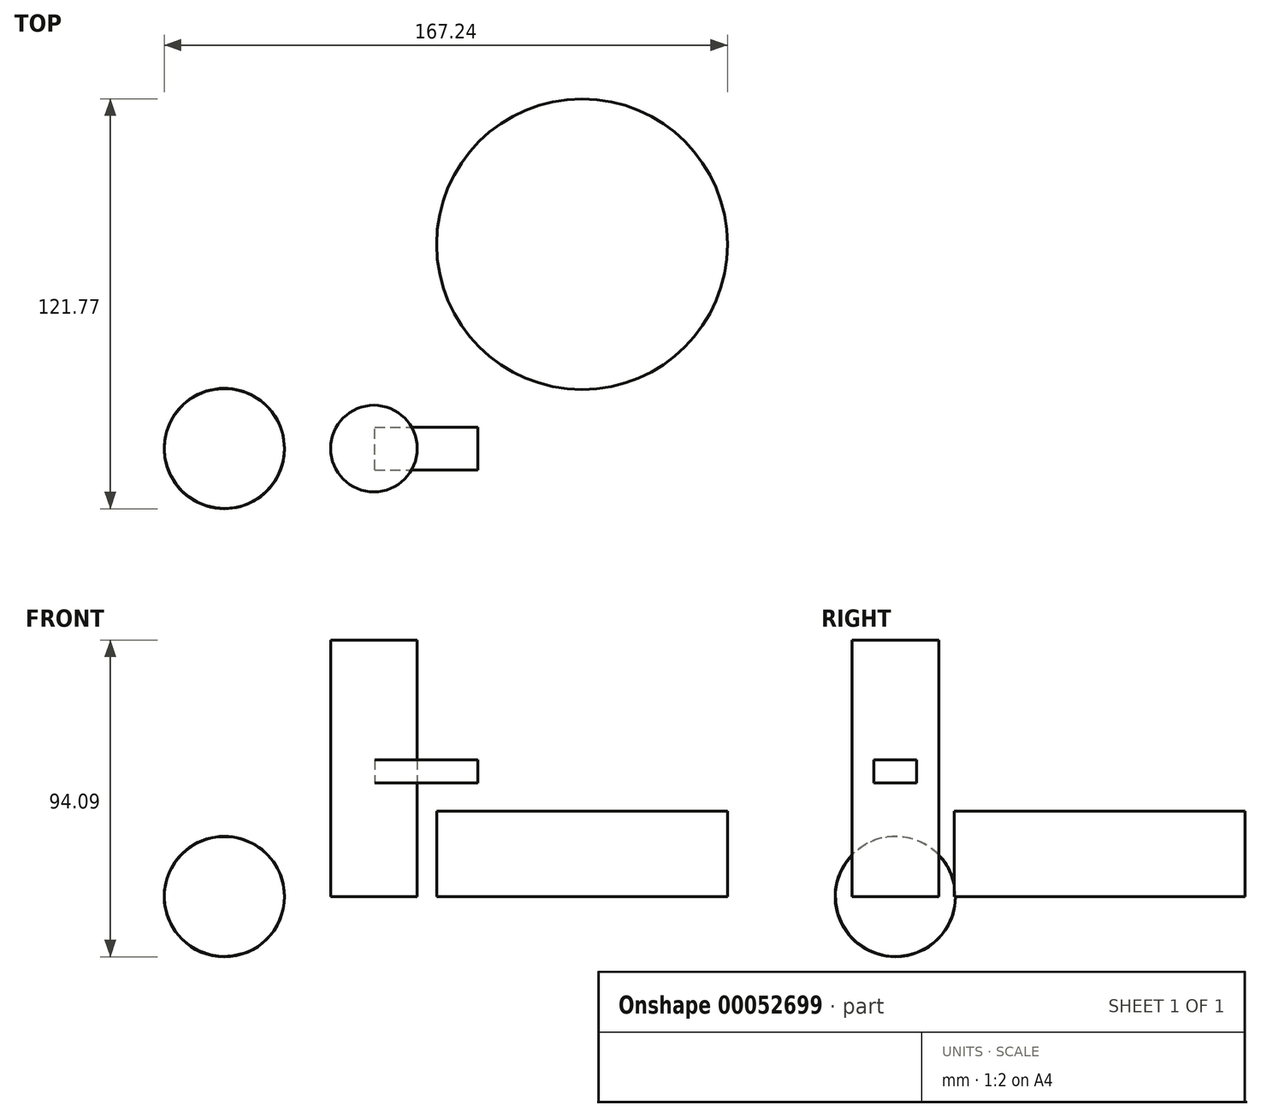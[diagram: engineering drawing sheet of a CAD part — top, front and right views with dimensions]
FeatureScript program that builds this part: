
annotation { "Feature Type Name" : "Feature", "Feature Type Description" : "" }
export const myFeature = defineFeature(function(context is Context, id is Id, definition is map)
    precondition{}
    {
        {
            var Q0;
            Q0=qCreatedBy(makeId("Front.planeOp"),FACE);
            var sketch = newSketch(context, id + "F0", { "sketchPlane" : qUnion([Q0])});
            skArc(sketch, "E0", {"start": v(-62.28, 0) * mm, "mid": v(-44.43, -17.89) * mm, "end": v(-26.59, 0) * mm});
            skLineSegment(sketch, "E1", {"start": v(-26.59, 0) * mm, "end": v(-62.28, 0) * mm});
            skSolve(sketch);
        }
        {
            var Q0;
            Q0 = qSketchRegion(id + "F0", true);
            var Q1;
            Q1=sQuery(id+"F0.wireOp",EDGE,"E1");
            revolve(context, id + "F1", {"entities" : qUnion([Q0]), "axis" : qUnion([Q1]), "revolveType" : RevolveType.FULL});
        }
        {
            var Q0;
            Q0=qCreatedBy(makeId("Top.planeOp"),FACE);
            var sketch = newSketch(context, id + "F2", { "sketchPlane" : qUnion([Q0])});
            skCircle(sketch, "E2", {"center": v(0, 0) * mm, "radius": 12.87 * mm});
            skSolve(sketch);
        }
        {
            var Q0;
            Q0 = qSketchRegion(id + "F2", true);
            extrude(context, id + "F3", {"entities" : qUnion([Q0]), "depth" : 76.2 * mm});
        }
        {
            var Q0;
            Q0=qCreatedBy(makeId("Top.planeOp"),FACE);
            var sketch = newSketch(context, id + "F4", { "sketchPlane" : qUnion([Q0])});
            skCircle(sketch, "E3", {"center": v(61.8, 60.7) * mm, "radius": 43.17 * mm});
            skSolve(sketch);
        }
        {
            var Q0;
            Q0 = qSketchRegion(id + "F4", true);
            extrude(context, id + "F5", {"entities" : qUnion([Q0]), "depth" : 25.4 * mm});
        }
        {
            var Q0;
            Q0=qCreatedBy(makeId("Front.planeOp"),FACE);
            var sketch = newSketch(context, id + "F6", { "sketchPlane" : qUnion([Q0])});
            skLineSegment(sketch, "E4.bottom", {"start": v(12.98, -33) * mm, "end": v(43.5, -33) * mm});
            skLineSegment(sketch, "E4.top", {"start": v(12.98, -39.85) * mm, "end": v(43.5, -39.85) * mm});
            skLineSegment(sketch, "E4.left", {"start": v(12.98, -33) * mm, "end": v(12.98, -39.85) * mm});
            skLineSegment(sketch, "E4.right", {"start": v(43.5, -33) * mm, "end": v(43.5, -39.85) * mm});
            skSolve(sketch);
        }
        {
            var Q0;
            Q0 = qSketchRegion(id + "F6", true);
            extrude(context, id + "F7", {"entities" : qUnion([Q0]), "depth" : 12.7 * mm});
        }
        {
            var Q0;
            Q0=makeQuery(id+"F7.opExtrude","SWEPT_BODY",BODY,{"disambiguationData":[OSD([sQuery(id+"F6.wireOp",EDGE,"E4.bottom"),sQuery(id+"F6.wireOp",EDGE,"E4.top"),sQuery(id+"F6.wireOp",EDGE,"E4.left"),sQuery(id+"F6.wireOp",EDGE,"E4.right")])]});
            transform(context, id + "F8", {"entities" : qUnion([Q0]), "transformType" : TransformType.TRANSLATION_3D, "dx" : -12.7 * mm, "dy" : 6.35 * mm, "dz" : 73.66 * mm, "makeCopy" : false});
        }
    });
